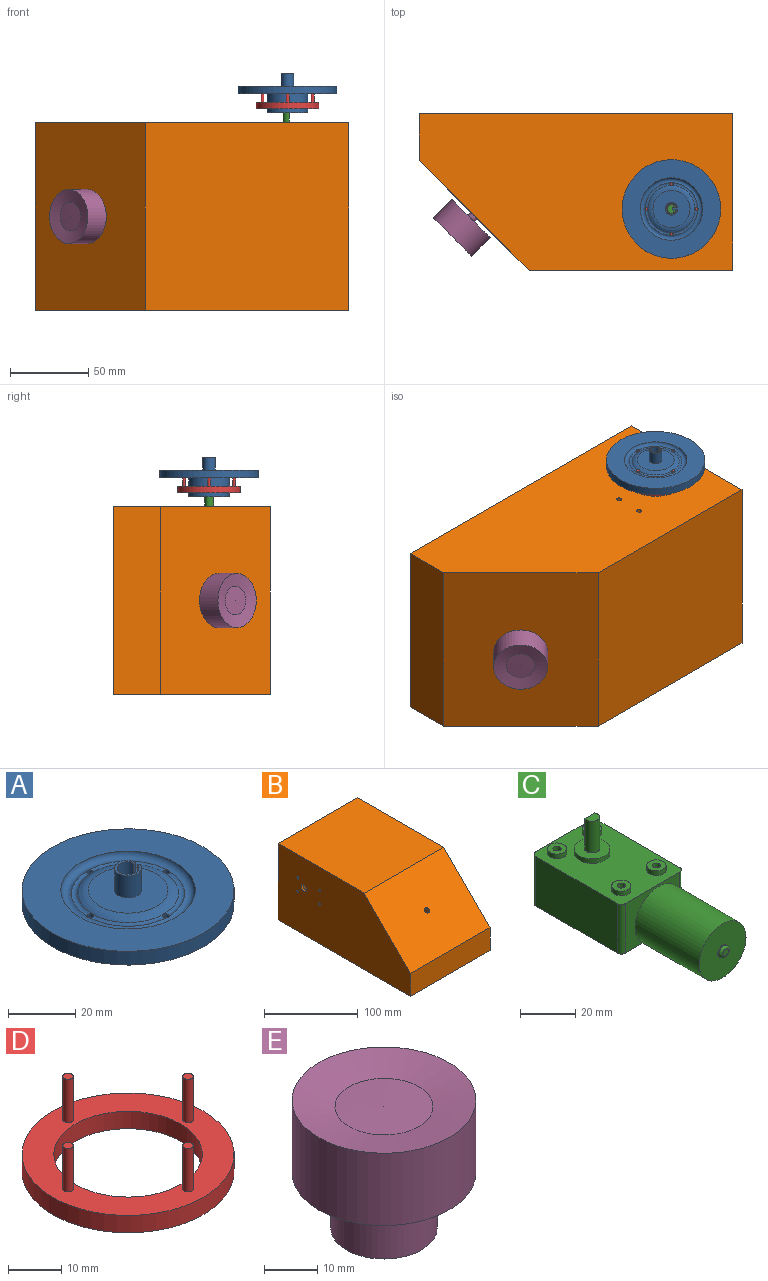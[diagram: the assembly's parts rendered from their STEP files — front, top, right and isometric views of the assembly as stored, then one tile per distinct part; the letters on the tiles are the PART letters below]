
ASSEMBLY  parts=5 mates=4
PART A: 29 faces, bbox 63x63x25 mm
  f0: cylinder r=13mm len=26mm, axis (0,0,1), area 980.2mm2, adj f9,f26
  f1: plane 10x2.36mm, normal (0,-1,0), area 17.3mm2, adj f2,f15,f19,f23,f27,f28
  f2: plane 7x1.31mm, normal (-1,0,0), area 9.2mm2, adj f1,f3,f23,f27
  f3: plane 10x2.32mm, normal (0,1,0), area 17.1mm2, adj f2,f15,f19,f23,f27,f28
  f4: torus R=16mm, axis (0,0,1), area 43.2mm2, adj f10,f13,f24,f25
  f5: torus R=16mm, axis (0,0,1), area 43.2mm2, adj f11,f13,f24,f25
  f6: torus R=16mm, axis (0,0,1), area 43.2mm2, adj f11,f12,f24,f25
  f7: plane 62.98x62.98mm, normal (0,0,1), area 1861.2mm2, adj f8,f24
  f8: cylinder r=31.49mm len=62.98mm, axis (0,0,1), area 989.2mm2, adj f7,f9
  f9: plane 62.98x62.98mm, normal (0,0,-1), area 2571.5mm2, adj f0,f8,f10,f11,f12,f13
  f10: cylinder r=1mm len=3.88mm, axis (0,0,-1), area 22.9mm2, adj f4,f9,f14,f24,f25
  f11: cylinder r=1mm len=3.88mm, axis (0,0,-1), area 22.9mm2, adj f5,f6,f9,f24,f25
  f12: cylinder r=1mm len=3.88mm, axis (0,0,-1), area 22.9mm2, adj f6,f9,f14,f24,f25
  f13: cylinder r=1mm len=3.88mm, axis (0,0,-1), area 22.9mm2, adj f4,f5,f9,f24,f25
  f14: torus R=16mm, axis (0,0,1), area 43.2mm2, adj f10,f12,f24,f25
  f15: plane 6.52x6.47mm, normal (0,0,1), area 4.8mm2, adj f1,f3,f19,f28
  f16: cylinder r=1mm len=1.17mm, axis (1,0,0), area 1.2mm2, adj f17,f19,f20,f21
  f17: plane 8x7.68mm, normal (0,0,1), area 14.3mm2, adj f16,f18,f19,f21
  f18: cylinder r=1mm len=1.1mm, axis (-1,0,0), area 1.2mm2, adj f17,f19,f21,f22
  f19: cylinder r=3.26mm len=18mm, axis (0,0,1), area 344.7mm2, adj f1,f3,f15,f16,f17,f18,f20,f22
  f20: plane 7x0.75mm, normal (0,-1,0), area 5.3mm2, adj f16,f19,f21,f23
  f21: cylinder r=4mm len=8mm, axis (0,0,-1), area 190.1mm2, adj f16,f17,f18,f20,f22,f23
  f22: plane 7x0.75mm, normal (0,1,0), area 5.2mm2, adj f18,f19,f21,f23
  f23: plane 23.69x23.69mm, normal (0,0,1), area 394.7mm2, adj f1,f2,f3,f20,f21,f22,f25
  f24: torus R=18mm, axis (0,0,1), area 485.6mm2, adj f4,f5,f6,f7,f10,f11,f12,f13
  f25: torus R=11.85mm, axis (0,0,-1), area 294.1mm2, adj f4,f5,f6,f10,f11,f12,f13,f14
  f26: plane 26x26mm, normal (0,0,-1), area 502.7mm2, adj f0,f28
  f27: plane 2.15x1.31mm, normal (0,0,-1), area 2.8mm2, adj f1,f2,f3,f28
  f28: cylinder r=3mm len=10mm, axis (0,0,-1), area 135.9mm2, adj f1,f3,f15,f26,f27
PART B: 19 faces, bbox 120x200x100 mm
  f0: plane 200x120mm, normal (0,0,-1), area 1884mm2, adj f1,f2,f3,f4,f7,f8,f9,f10
  f1: plane 120x30mm, normal (0,-1,0), area 3600mm2, adj f0,f2,f4,f6
  f2: plane 200x100mm, normal (1,0,0), area 17550mm2, adj f0,f1,f3,f5,f6
  f3: plane 120x100mm, normal (0,1,0), area 12000mm2, adj f0,f2,f4,f5
  f4: plane 200x100mm, normal (-1,0,0), area 17471.5mm2, adj f0,f1,f3,f5,f6,f13,f14,f15
  f5: plane 130x120mm, normal (0,0,1), area 15600mm2, adj f2,f3,f4,f6
  f6: plane 120x70mm, normal (0,-0.71,0.71), area 11851.1mm2, adj f1,f2,f4,f5,f18
  f7: plane 114x28.76mm, normal (0,1,0), area 3278.3mm2, adj f0,f8,f10,f12
  f8: plane 194x97mm, normal (-1,0,0), area 16489.5mm2, adj f0,f7,f9,f11,f12
  f9: plane 114x97mm, normal (0,-1,0), area 11058mm2, adj f0,f8,f10,f11
  f10: plane 194x97mm, normal (1,0,0), area 16410.9mm2, adj f0,f7,f9,f11,f12,f13,f14,f15
  f11: plane 125.76x114mm, normal (0,0,-1), area 14336.3mm2, adj f8,f9,f10,f12
  f12: plane 114x68.24mm, normal (0,0.71,-0.71), area 10973.8mm2, adj f7,f8,f10,f11,f18
  f13: cylinder r=1.5mm len=3mm, axis (-1,0,0), area 28.3mm2, adj f4,f10
  f14: cylinder r=1.5mm len=3mm, axis (-1,0,0), area 28.3mm2, adj f4,f10
  f15: cylinder r=1.5mm len=3mm, axis (-1,0,0), area 28.3mm2, adj f4,f10
  f16: cylinder r=1.5mm len=3mm, axis (-1,0,0), area 28.3mm2, adj f4,f10
  f17: cylinder r=4mm len=8mm, axis (-1,0,0), area 75.4mm2, adj f4,f10
  f18: cylinder r=3mm len=6.36mm, axis (0,-0.71,0.71), area 56.5mm2, adj f6,f12
PART C: 40 faces, bbox 32x80.5x41 mm
  f0: plane 4.2x3.06mm, normal (0,-1,0), area 5.4mm2, adj f6,f28,f34
  f1: plane 28x22mm, normal (0,-1,0), area 197.3mm2, adj f5,f6,f28,f36,f39
  f2: plane 42.27x22mm, normal (1,0,0), area 925.3mm2, adj f5,f6,f34,f35,f36,f37
  f3: plane 28x22mm, normal (0,1,0), area 616mm2, adj f5,f6,f37,f38
  f4: plane 42x22mm, normal (-1,0,0), area 924mm2, adj f5,f6,f38,f39
  f5: plane 46x32mm, normal (0,0,1), area 1181.9mm2, adj f1,f2,f3,f4,f7,f13,f17,f21
  f6: plane 46x32mm, normal (0,0,-1), area 1468.6mm2, adj f0,f1,f2,f3,f4,f30,f34,f37
  f7: cylinder r=6.5mm len=13mm, axis (0,0,-1), area 81.7mm2, adj f5,f8
  f8: plane 13x13mm, normal (0,0,1), area 114.7mm2, adj f7,f9,f10
  f9: cylinder r=2.75mm len=14mm, axis (0,0,-1), area 154mm2, adj f8,f10,f11
  f10: plane 14x5mm, normal (0,1,0), area 70mm2, adj f8,f9,f11
  f11: plane 5.5x3.9mm, normal (0,0,1), area 18mm2, adj f9,f10
  f12: cylinder r=1.5mm len=3mm, axis (0,0,-1), area 18.8mm2, adj f14,f15
  f13: cylinder r=3.5mm len=7mm, axis (0,0,-1), area 44mm2, adj f5,f14
  f14: plane 7x7mm, normal (0,0,1), area 31.4mm2, adj f12,f13
  f15: plane 3x3mm, normal (0,0,1), area 7.1mm2, adj f12
  f16: cylinder r=1.5mm len=3mm, axis (0,0,-1), area 18.8mm2, adj f18,f19
  f17: cylinder r=3.5mm len=7mm, axis (0,0,-1), area 44mm2, adj f5,f18
  f18: plane 7x7mm, normal (0,0,1), area 31.4mm2, adj f16,f17
  f19: plane 3x3mm, normal (0,0,1), area 7.1mm2, adj f16
  f20: cylinder r=1.5mm len=3mm, axis (0,0,-1), area 18.8mm2, adj f22,f23
  f21: cylinder r=3.5mm len=7mm, axis (0,0,-1), area 44mm2, adj f5,f22
  f22: plane 7x7mm, normal (0,0,1), area 31.4mm2, adj f20,f21
  f23: plane 3x3mm, normal (0,0,1), area 7.1mm2, adj f20
  f24: cylinder r=1.5mm len=3mm, axis (0,0,-1), area 18.8mm2, adj f26,f27
  f25: cylinder r=3.5mm len=7mm, axis (0,0,-1), area 44mm2, adj f5,f26
  f26: plane 7x7mm, normal (0,0,1), area 31.4mm2, adj f24,f25
  f27: plane 3x3mm, normal (0,0,1), area 7.1mm2, adj f24
  f28: cylinder r=12mm len=33mm, axis (0,1,0), area 2488.1mm2, adj f0,f1,f29,f30,f35
  f29: plane 24x24mm, normal (0,-1,0), area 432.8mm2, adj f28,f31
  f30: plane 15.87x3mm, normal (0,1,0), area 32.6mm2, adj f6,f28
  f31: cylinder r=2.5mm len=5mm, axis (0,1,0), area 7.9mm2, adj f29,f33
  f32: plane 3x3mm, normal (0,-1,0), area 7.1mm2, adj f33
  f33: torus R=1.5mm, axis (0,-1,0), area 21.1mm2, adj f31,f32
  f34: cylinder r=2mm len=4.2mm, axis (0,0,1), area 13.2mm2, adj f0,f2,f6,f35
  f35: bspline ~10.6x2.34mm, area 23.5mm2, adj f2,f28,f34,f36
  f36: cylinder r=2mm len=8.2mm, axis (0,0,1), area 25.8mm2, adj f1,f2,f5,f35
  f37: cylinder r=2mm len=22mm, axis (0,0,-1), area 69.1mm2, adj f2,f3,f5,f6
  f38: cylinder r=2mm len=22mm, axis (0,0,1), area 69.1mm2, adj f3,f4,f5,f6
  f39: cylinder r=2mm len=22mm, axis (0,0,-1), area 69.1mm2, adj f1,f4,f5,f6
PART D: 12 faces, bbox 40x40x14 mm
  f0: cylinder r=14mm len=28mm, axis (0,0,-1), area 351.9mm2, adj f2,f3
  f1: cylinder r=20mm len=40mm, axis (0,0,-1), area 502.7mm2, adj f2,f3
  f2: plane 40x40mm, normal (0,0,1), area 628.3mm2, adj f0,f1,f4,f6,f8,f10
  f3: plane 40x40mm, normal (0,0,-1), area 640.9mm2, adj f0,f1
  f4: cylinder r=1mm len=10mm, axis (0,0,-1), area 62.8mm2, adj f2,f5
  f5: plane 2x2mm, normal (0,0,1), area 3.1mm2, adj f4
  f6: cylinder r=1mm len=10mm, axis (0,0,-1), area 62.8mm2, adj f2,f7
  f7: plane 2x2mm, normal (0,0,1), area 3.1mm2, adj f6
  f8: cylinder r=1mm len=10mm, axis (0,0,-1), area 62.8mm2, adj f2,f9
  f9: plane 2x2mm, normal (0,0,1), area 3.1mm2, adj f8
  f10: cylinder r=1mm len=10mm, axis (0,0,-1), area 62.8mm2, adj f2,f11
  f11: plane 2x2mm, normal (0,0,1), area 3.1mm2, adj f10
PART E: 8 faces, bbox 34.6x34.6x29.5 mm
  f0: cylinder r=10mm len=20mm, axis (0,0,-1), area 628.3mm2, adj f1,f2
  f1: plane 20x20mm, normal (0,0,1), area 285.9mm2, adj f0,f3
  f2: plane 20x20mm, normal (0,0,-1), area 314.2mm2, adj f0
  f3: cylinder r=3mm len=6mm, axis (0,0,-1), area 54mm2, adj f1,f7
  f4: cone r=9.22mm half-angle=89.4deg, axis (0,0,-1), area 267.3mm2, adj f5
  f5: cone r=17.31mm half-angle=79.4deg, axis (0,0,1), area 685.7mm2, adj f4,f6
  f6: cylinder r=17.31mm len=34.62mm, axis (0,0,-1), area 1813.5mm2, adj f5,f7
  f7: plane 34.62x34.62mm, normal (0,0,-1), area 912.9mm2, adj f3,f6
PLACE A t=(35.55,-190.9,1.81)mm
PLACE B rot(axis=(0.58,0.58,-0.58),120deg) t=(-25.45,-129.9,-64.55)mm
PLACE C rot(axis=(0,0,-1),90deg) t=(35.55,-190.9,-31.55)mm
PLACE D t=(35.55,-190.9,4.45)mm
PLACE E rot(axis=(0.86,-0.36,-0.36),98.4deg) t=(-83.38,-187.83,-64.55)mm
MATE fastened B.f18 <-> E.f0  axis (-0.71,-0.71,0) through (-90.45,-194.9,-64.55)mm
MATE slider D.f4 <-> A.f10  axis (0,0,-1) through (35.55,-174.9,18.45)mm
MATE revolute C.f9 <-> D.f1  axis (0,0,1) through (35.55,-190.9,6.45)mm
MATE fastened C.f12 <-> B.f14  axis (0,0,1) through (44.55,-181.9,-7.55)mm
